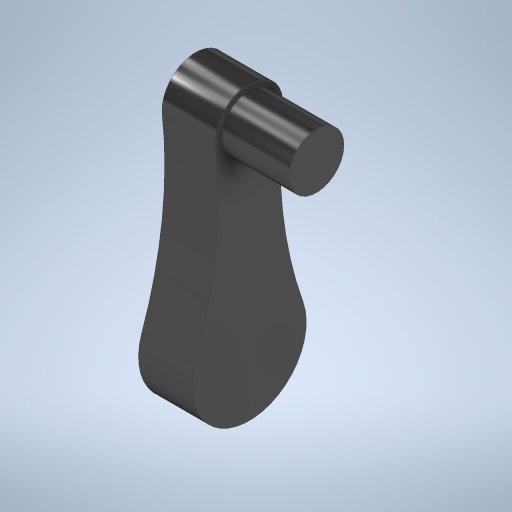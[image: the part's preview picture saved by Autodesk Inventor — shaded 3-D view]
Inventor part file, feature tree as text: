
AUTODESK INVENTOR PART (.ipt)
format: ipt  version: 2023 (Build 270158000, 158)  size: 273,408 bytes
history: native  units: mm
features: extrude x3, sketch x3
ambient origin geometry x8: Origin, YZ Plane, XZ Plane, XY Plane, X Axis, Y Axis, Z Axis, Center Point
bodies: Volumenkörper1 (feature_tree)
feature tree (6):
  extrude  "Extrusion1"  Depth=10.0mm
  extrude  "Extrusion2"  Depth=60.0mm
  extrude  "Extrusion4"  TaperAngle=0.0deg  [1 undecoded]
  sketch  "Skizze1"  dims[d0=10.0mm d1=17.0mm]
  sketch  "Skizze2"  dims[d2=30.0mm d3=60.0mm]
  sketch  "Skizze4"  dims[d4=0.0mm d5=0.0mm d6=60.0mm d7=8.0mm d8=0.0mm d9=8.2mm d10=10.0mm d11=0.0mm d15=12.1mm d16=6.0mm d17=0.0mm]
note: 1 required parameter value undecoded (feature->parameter linkage not recoverable at this tier; creation-order binding heuristic only, values carry confidence <= 0.55)
